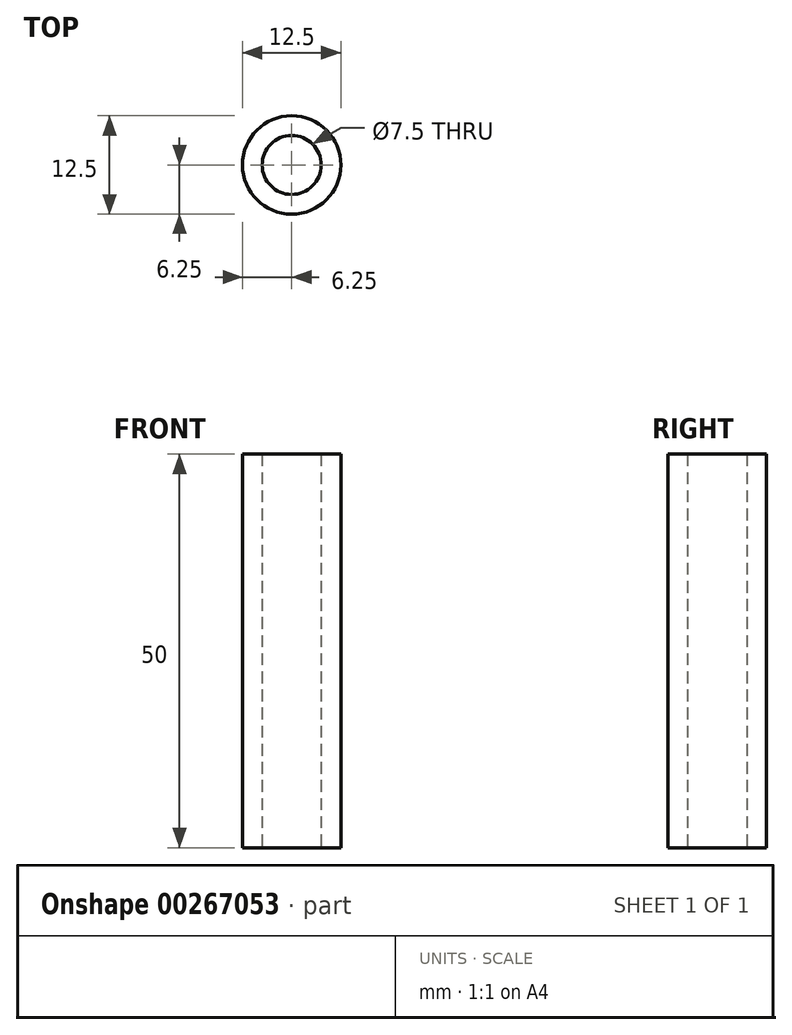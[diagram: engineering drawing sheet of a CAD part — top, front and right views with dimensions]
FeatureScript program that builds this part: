
annotation { "Feature Type Name" : "Feature", "Feature Type Description" : "" }
export const myFeature = defineFeature(function(context is Context, id is Id, definition is map)
    precondition{}
    {
        {
            var Q0;
            Q0=qCreatedBy(makeId("Top.planeOp"),FACE);
            var sketch = newSketch(context, id + "F0", { "sketchPlane" : qUnion([Q0])});
            skCircle(sketch, "E0", {"center": v(0, 0) * mm, "radius": 6.25 * mm});
            skCircle(sketch, "E1", {"center": v(0, 0) * mm, "radius": 3.75 * mm});
            skSolve(sketch);
        }
        {
            var Q0;
            Q0=makeQuery(id+"F0.imprint","IMPRINT",FACE,{"disambiguationData":[TD([[makeQuery(id+"F0.imprint","IMPRINT",EDGE,{"derivedFrom":sQuery(id+"F0.wireOp",EDGE,"E0")}),1.0]])]});
            extrude(context, id + "F1", {"entities" : qUnion([Q0]), "depth" : 50 * mm});
        }
    });
